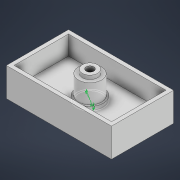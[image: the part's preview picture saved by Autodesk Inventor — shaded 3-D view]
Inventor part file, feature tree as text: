
AUTODESK INVENTOR PART (.ipt)
format: ipt  version: 2021 (Build 250183000, 183)  size: 134,144 bytes
history: native  units: mm
features: extrude x6, sketch x5
ambient origin geometry x8: Origin, YZ Plane, XZ Plane, XY Plane, X Axis, Y Axis, Z Axis, Center Point
bodies: Volumenkörper1 (feature_tree)
feature tree (11):
  extrude  "Extrusion1"  Depth=32.5mm
  extrude  "Extrusion5"  Depth=2.0mm
  sketch  "Skizze6"  dims[d15=10.0mm d16=0.0mm d17=12.0mm]
  extrude  "Extrusion6"  Depth=12.0mm
  extrude  "Extrusion7"  Depth=2.0mm TaperAngle=0.0deg
  extrude  "Extrusion8"  Depth=4.0mm
  extrude  "Extrusion9"  Depth=2.0mm TaperAngle=0.0deg
  sketch  "Skizze1"  dims[d0=55.0mm d1=32.5mm]
  sketch  "Skizze5"  dims[d2=5.0mm d3=0.0mm d14=2.0mm]
  sketch  "Skizze8"  dims[d18=14.0mm d19=2.0mm d20=0.0mm]
  sketch  "Skizze9"  dims[d21=12.0mm d22=0.0mm d23=7.9mm d24=2.0mm d25=0.0mm d26=4.0mm d27=4.0mm d28=0.0mm]
